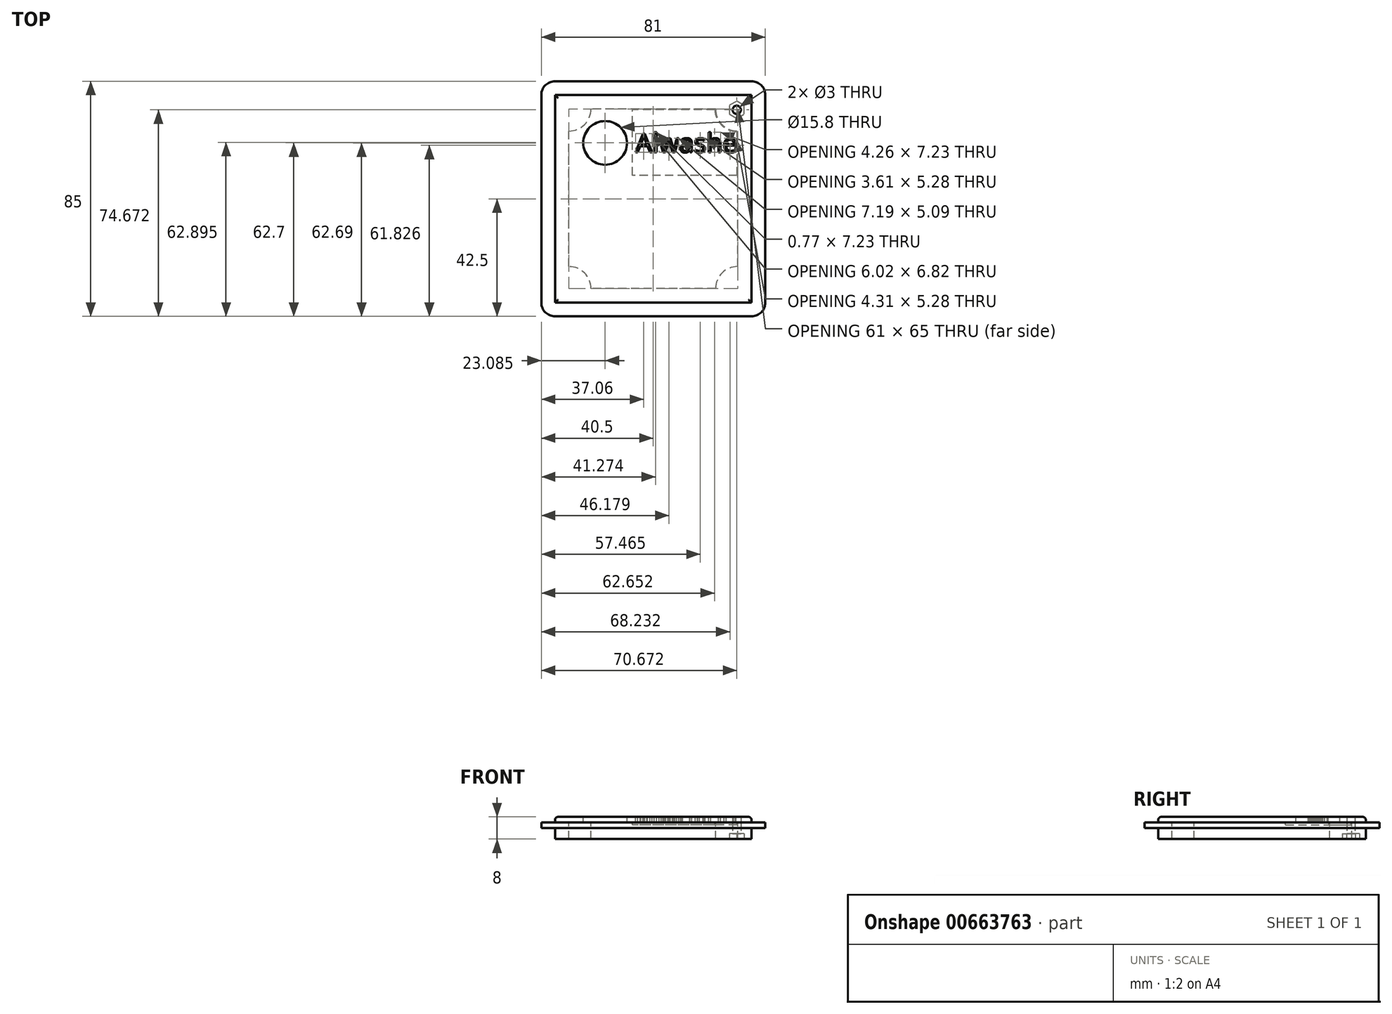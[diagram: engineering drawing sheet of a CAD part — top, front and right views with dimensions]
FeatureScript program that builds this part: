
annotation { "Feature Type Name" : "Feature", "Feature Type Description" : "" }
export const myFeature = defineFeature(function(context is Context, id is Id, definition is map)
    precondition{}
    {
        {
            var Q0;
            Q0=qCreatedBy(makeId("Top.planeOp"),FACE);
            var sketch = newSketch(context, id + "F0", { "sketchPlane" : qUnion([Q0])});
            skLineSegment(sketch, "E0.bottom", {"start": v(35.5, -37.5) * mm, "end": v(-35.5, -37.5) * mm});
            skLineSegment(sketch, "E0.top", {"start": v(35.5, 37.5) * mm, "end": v(-35.5, 37.5) * mm});
            skLineSegment(sketch, "E0.left", {"start": v(35.5, -37.5) * mm, "end": v(35.5, 37.5) * mm});
            skLineSegment(sketch, "E0.right", {"start": v(-35.5, -37.5) * mm, "end": v(-35.5, 37.5) * mm});
            skPoint(sketch, "E0.middle", {"position": v(0, 0) * mm});
            skSolve(sketch);
        }
        {
            var Q0;
            Q0 = qSketchRegion(id + "F0", true);
            extrude(context, id + "F1", {"entities" : qUnion([Q0]), "depth" : 4 * mm, "offsetDistance" : 25 * mm});
        }
        {
            var Q0;
            Q0=makeQuery(id+"F1.opExtrude","CAP_FACE",FACE,{"disambiguationData":[OSD([sQuery(id+"F0.wireOp",EDGE,"E0.bottom"),sQuery(id+"F0.wireOp",EDGE,"E0.top"),sQuery(id+"F0.wireOp",EDGE,"E0.left"),sQuery(id+"F0.wireOp",EDGE,"E0.right")])],"isStart":false});
            var sketch = newSketch(context, id + "F2", { "sketchPlane" : qUnion([Q0])});
            skLineSegment(sketch, "E1.bottom", {"start": v(30.5, -32.5) * mm, "end": v(22.5, -32.5) * mm, "construction": true});
            skLineSegment(sketch, "E1.top", {"start": v(30.5, 32.5) * mm, "end": v(22.5, 32.5) * mm, "construction": true});
            skLineSegment(sketch, "E1.left", {"start": v(30.5, -32.5) * mm, "end": v(30.5, -24.5) * mm, "construction": true});
            skLineSegment(sketch, "E1.right", {"start": v(-30.5, -32.5) * mm, "end": v(-30.5, -24.5) * mm, "construction": true});
            skPoint(sketch, "E1.middle", {"position": v(0, 0) * mm});
            skArc(sketch, "E2", {"start": v(-30.5, 24.5) * mm, "mid": v(-24.84, 26.84) * mm, "end": v(-22.5, 32.5) * mm});
            skLineSegment(sketch, "E3", {"start": v(-22.5, 32.5) * mm, "end": v(-30.5, 32.5) * mm, "construction": true});
            skLineSegment(sketch, "E4", {"start": v(-30.5, 24.5) * mm, "end": v(-30.5, 32.5) * mm, "construction": true});
            skArc(sketch, "E5.MirrorCS", {"start": v(30.5, 24.5) * mm, "mid": v(24.84, 26.84) * mm, "end": v(22.5, 32.5) * mm});
            skArc(sketch, "E6.MirrorCS", {"start": v(-30.5, -24.5) * mm, "mid": v(-24.84, -26.84) * mm, "end": v(-22.5, -32.5) * mm});
            skArc(sketch, "E7.MirrorCS", {"start": v(30.5, -24.5) * mm, "mid": v(24.84, -26.84) * mm, "end": v(22.5, -32.5) * mm});
            skLineSegment(sketch, "E8", {"start": v(-30.5, -24.5) * mm, "end": v(-30.5, 24.5) * mm});
            skLineSegment(sketch, "E9", {"start": v(-22.5, -32.5) * mm, "end": v(-30.5, -32.5) * mm, "construction": true});
            skLineSegment(sketch, "E10", {"start": v(22.5, -32.5) * mm, "end": v(-22.5, -32.5) * mm});
            skLineSegment(sketch, "E11", {"start": v(30.5, -24.5) * mm, "end": v(30.5, 24.5) * mm});
            skLineSegment(sketch, "E12", {"start": v(30.5, 24.5) * mm, "end": v(30.5, 32.5) * mm, "construction": true});
            skLineSegment(sketch, "E13", {"start": v(22.5, 32.5) * mm, "end": v(-22.5, 32.5) * mm});
            skSolve(sketch);
        }
        {
            var Q0;
            Q0=makeQuery(id+"F2.imprint","IMPRINT",FACE,{"disambiguationData":[TD([[makeQuery(id+"F2.imprint","IMPRINT",EDGE,{"derivedFrom":sQuery(id+"F2.wireOp",EDGE,"E2")}),-1.0]])]});
            extrude(context, id + "F3", {"entities" : qUnion([Q0]), "operationType" : NewBodyOperationType.REMOVE, "oppositeDirection" : true, "depth" : 25 * mm, "offsetDistance" : 25 * mm});
        }
        {
            var Q0;
            Q0=makeQuery(id+"F1.opExtrude","CAP_FACE",FACE,{"disambiguationData":[OSD([sQuery(id+"F0.wireOp",EDGE,"E0.bottom"),sQuery(id+"F0.wireOp",EDGE,"E0.top"),sQuery(id+"F0.wireOp",EDGE,"E0.left"),sQuery(id+"F0.wireOp",EDGE,"E0.right")])],"isStart":false});
            var sketch = newSketch(context, id + "F4", { "sketchPlane" : qUnion([Q0])});
            skLineSegment(sketch, "E14.bottom", {"start": v(35.5, -42.5) * mm, "end": v(-35.5, -42.5) * mm});
            skLineSegment(sketch, "E14.top", {"start": v(35.5, 42.5) * mm, "end": v(-35.5, 42.5) * mm});
            skLineSegment(sketch, "E14.left", {"start": v(40.5, -37.5) * mm, "end": v(40.5, 37.5) * mm});
            skLineSegment(sketch, "E14.right", {"start": v(-40.5, -37.5) * mm, "end": v(-40.5, 37.5) * mm});
            skPoint(sketch, "E14.middle", {"position": v(0, 0) * mm});
            skPoint(sketch, "E15.visualSharp", {"position": v(-40.5, 42.5) * mm});
            skArc(sketch, "E15.filletArc", {"start": v(-35.5, 42.5) * mm, "mid": v(-39.04, 41.04) * mm, "end": v(-40.5, 37.5) * mm});
            skPoint(sketch, "E16.visualSharp", {"position": v(40.5, 42.5) * mm});
            skArc(sketch, "E16.filletArc", {"start": v(40.5, 37.5) * mm, "mid": v(39.04, 41.04) * mm, "end": v(35.5, 42.5) * mm});
            skPoint(sketch, "E17.visualSharp", {"position": v(40.5, -42.5) * mm});
            skArc(sketch, "E17.filletArc", {"start": v(35.5, -42.5) * mm, "mid": v(39.04, -41.04) * mm, "end": v(40.5, -37.5) * mm});
            skPoint(sketch, "E18.visualSharp", {"position": v(-40.5, -42.5) * mm});
            skArc(sketch, "E18.filletArc", {"start": v(-40.5, -37.5) * mm, "mid": v(-39.04, -41.04) * mm, "end": v(-35.5, -42.5) * mm});
            skArc(sketch, "E19.0", {"start": v(-30.5, 24.5) * mm, "mid": v(-24.84, 26.84) * mm, "end": v(-22.5, 32.5) * mm});
            skLineSegment(sketch, "E19.1", {"start": v(22.5, 32.5) * mm, "end": v(-22.5, 32.5) * mm});
            skArc(sketch, "E19.2", {"start": v(30.5, 24.5) * mm, "mid": v(24.84, 26.84) * mm, "end": v(22.5, 32.5) * mm});
            skLineSegment(sketch, "E19.3", {"start": v(30.5, -24.5) * mm, "end": v(30.5, 24.5) * mm});
            skArc(sketch, "E19.4", {"start": v(30.5, -24.5) * mm, "mid": v(24.84, -26.84) * mm, "end": v(22.5, -32.5) * mm});
            skLineSegment(sketch, "E19.5", {"start": v(22.5, -32.5) * mm, "end": v(-22.5, -32.5) * mm});
            skArc(sketch, "E19.6", {"start": v(-30.5, -24.5) * mm, "mid": v(-24.84, -26.84) * mm, "end": v(-22.5, -32.5) * mm});
            skLineSegment(sketch, "E19.7", {"start": v(-30.5, -24.5) * mm, "end": v(-30.5, 24.5) * mm});
            skSolve(sketch);
        }
        {
            var Q0;
            Q0 = qSketchRegion(id + "F4", true);
            extrude(context, id + "F5", {"entities" : qUnion([Q0]), "operationType" : NewBodyOperationType.ADD, "depth" : 2 * mm, "offsetDistance" : 25 * mm});
        }
        {
            var Q0;
            Q0=makeQuery(id+"F1.opExtrude","CAP_FACE",FACE,{"disambiguationData":[OSD([sQuery(id+"F0.wireOp",EDGE,"E0.bottom"),sQuery(id+"F0.wireOp",EDGE,"E0.top"),sQuery(id+"F0.wireOp",EDGE,"E0.left"),sQuery(id+"F0.wireOp",EDGE,"E0.right")])],"isStart":true});
            var sketch = newSketch(context, id + "F6", { "sketchPlane" : qUnion([Q0])});
            skLineSegment(sketch, "E20", {"start": v(35.5, -37.5) * mm, "end": v(24.84, -26.84) * mm, "construction": true});
            skCircle(sketch, "E21.cCircle", {"center": v(30.17, -32.17) * mm, "radius": 2.7 * mm, "construction": true});
            skLineSegment(sketch, "E21.0", {"start": v(27.47, -33.73) * mm, "end": v(27.47, -30.61) * mm});
            skLineSegment(sketch, "E21.1", {"start": v(27.47, -30.61) * mm, "end": v(30.17, -29.05) * mm});
            skLineSegment(sketch, "E21.2", {"start": v(30.17, -29.05) * mm, "end": v(32.87, -30.61) * mm});
            skLineSegment(sketch, "E21.3", {"start": v(32.87, -30.61) * mm, "end": v(32.87, -33.73) * mm});
            skLineSegment(sketch, "E21.4", {"start": v(32.87, -33.73) * mm, "end": v(30.17, -35.29) * mm});
            skLineSegment(sketch, "E21.5", {"start": v(30.17, -35.29) * mm, "end": v(27.47, -33.73) * mm});
            skPoint(sketch, "E21.0.midPoint", {"position": v(27.47, -32.17) * mm});
            skSolve(sketch);
        }
        {
            var Q0;
            Q0 = qSketchRegion(id + "F6", true);
            extrude(context, id + "F7", {"entities" : qUnion([Q0]), "operationType" : NewBodyOperationType.REMOVE, "oppositeDirection" : true, "depth" : 2 * mm, "offsetDistance" : 25 * mm});
        }
        {
            var Q0;
            Q0=makeQuery(id+"F5.opExtrude","CAP_FACE",FACE,{"disambiguationData":[OSD([sQuery(id+"F4.wireOp",EDGE,"E14.bottom"),sQuery(id+"F4.wireOp",EDGE,"E14.top"),sQuery(id+"F4.wireOp",EDGE,"E14.left"),sQuery(id+"F4.wireOp",EDGE,"E14.right"),sQuery(id+"F4.wireOp",EDGE,"E15.filletArc"),sQuery(id+"F4.wireOp",EDGE,"E16.filletArc"),sQuery(id+"F4.wireOp",EDGE,"E17.filletArc"),sQuery(id+"F4.wireOp",EDGE,"E18.filletArc"),sQuery(id+"F4.wireOp",EDGE,"E19.0"),sQuery(id+"F4.wireOp",EDGE,"E19.1"),sQuery(id+"F4.wireOp",EDGE,"E19.2"),sQuery(id+"F4.wireOp",EDGE,"E19.3"),sQuery(id+"F4.wireOp",EDGE,"E19.4"),sQuery(id+"F4.wireOp",EDGE,"E19.5"),sQuery(id+"F4.wireOp",EDGE,"E19.6"),sQuery(id+"F4.wireOp",EDGE,"E19.7")])],"isStart":false});
            var sketch = newSketch(context, id + "F8", { "sketchPlane" : qUnion([Q0])});
            skLineSegment(sketch, "E22.bottom", {"start": v(-35.5, 37.5) * mm, "end": v(35.5, 37.5) * mm});
            skLineSegment(sketch, "E22.top", {"start": v(-35.5, -37.5) * mm, "end": v(35.5, -37.5) * mm});
            skLineSegment(sketch, "E22.left", {"start": v(-35.5, 37.5) * mm, "end": v(-35.5, -37.5) * mm});
            skLineSegment(sketch, "E22.right", {"start": v(35.5, 37.5) * mm, "end": v(35.5, -37.5) * mm});
            skPoint(sketch, "E22.middle", {"position": v(0, 0) * mm});
            skLineSegment(sketch, "E23", {"start": v(-30.5, 0) * mm, "end": v(-40.5, 0) * mm});
            skPoint(sketch, "E24", {"position": v(-35.5, 0) * mm});
            skLineSegment(sketch, "E25", {"start": v(0, -42.5) * mm, "end": v(0, -32.5) * mm, "construction": true});
            skPoint(sketch, "E26", {"position": v(0, -37.5) * mm});
            skSolve(sketch);
        }
        {
            var Q0;
            Q0 = qSketchRegion(id + "F8", true);
            extrude(context, id + "F9", {"entities" : qUnion([Q0]), "depth" : 2 * mm, "offsetDistance" : 25 * mm});
        }
        {
            var Q0;
            Q0=makeQuery(id+"F1.opExtrude","CAP_FACE",FACE,{"disambiguationData":[OSD([sQuery(id+"F0.wireOp",EDGE,"E0.bottom"),sQuery(id+"F0.wireOp",EDGE,"E0.top"),sQuery(id+"F0.wireOp",EDGE,"E0.left"),sQuery(id+"F0.wireOp",EDGE,"E0.right")])],"isStart":true});
            var sketch = newSketch(context, id + "F10", { "sketchPlane" : qUnion([Q0])});
            skPoint(sketch, "E27.0", {"position": v(30.17, -32.17) * mm});
            skCircle(sketch, "E28", {"center": v(30.17, -32.17) * mm, "radius": 1.5 * mm});
            skSolve(sketch);
        }
        {
            var Q0;
            Q0 = qSketchRegion(id + "F10", true);
            extrude(context, id + "F11", {"entities" : qUnion([Q0]), "operationType" : NewBodyOperationType.REMOVE, "oppositeDirection" : true, "depth" : 25 * mm, "offsetDistance" : 25 * mm});
        }
        {
            var Q0;
            Q0=makeQuery(id+"F9.opExtrude","CAP_FACE",FACE,{"disambiguationData":[OSD([sQuery(id+"F8.wireOp",EDGE,"E22.bottom"),sQuery(id+"F8.wireOp",EDGE,"E22.top"),sQuery(id+"F8.wireOp",EDGE,"E22.left"),sQuery(id+"F8.wireOp",EDGE,"E22.right")])],"isStart":false});
            var sketch = newSketch(context, id + "F12", { "sketchPlane" : qUnion([Q0])});
            skCircle(sketch, "E29", {"center": v(-17.41, 20.2) * mm, "radius": 7.9 * mm});
            skCircle(sketch, "E30", {"center": v(-17.41, 0) * mm, "radius": 7.9 * mm, "construction": true});
            skCircle(sketch, "E31", {"center": v(-17.41, -20.2) * mm, "radius": 7.9 * mm, "construction": true});
            skLineSegment(sketch, "E32.0", {"start": v(22.5, 32.5) * mm, "end": v(-22.5, 32.5) * mm, "construction": true});
            skLineSegment(sketch, "E32.1", {"start": v(22.5, -32.5) * mm, "end": v(-22.5, -32.5) * mm, "construction": true});
            skLineSegment(sketch, "E32.2", {"start": v(-30.5, -24.5) * mm, "end": v(-30.5, 24.5) * mm, "construction": true});
            skArc(sketch, "E32.3", {"start": v(-30.5, -24.5) * mm, "mid": v(-24.84, -26.84) * mm, "end": v(-22.5, -32.5) * mm, "construction": true});
            skArc(sketch, "E32.4", {"start": v(-30.5, 24.5) * mm, "mid": v(-24.84, 26.84) * mm, "end": v(-22.5, 32.5) * mm, "construction": true});
            skArc(sketch, "E32.5", {"start": v(30.5, 24.5) * mm, "mid": v(24.84, 26.84) * mm, "end": v(22.5, 32.5) * mm, "construction": true});
            skLineSegment(sketch, "E32.6", {"start": v(30.5, -24.5) * mm, "end": v(30.5, 24.5) * mm, "construction": true});
            skArc(sketch, "E32.7", {"start": v(30.5, -24.5) * mm, "mid": v(24.84, -26.84) * mm, "end": v(22.5, -32.5) * mm, "construction": true});
            skLineSegment(sketch, "E33", {"start": v(-17.41, 32.5) * mm, "end": v(-17.41, 7.9) * mm, "construction": true});
            skText(sketch, "E34", { "text": "Alwashe", "fontName": "OpenSans-Regular.ttf"});
            skPoint(sketch, "E35", {"position": v(-6.45, 20.2) * mm});
            const initialGuessF12  = {"E34": [-0.00645, 0.01678, 1, 0, 0.00685]};
            skSetInitialGuess(sketch, initialGuessF12);
            skSolve(sketch);
        }
        {
            var Q0;
            Q0 = qSketchRegion(id + "F12", true);
            extrude(context, id + "F13", {"entities" : qUnion([Q0]), "operationType" : NewBodyOperationType.REMOVE, "oppositeDirection" : true, "depth" : 25 * mm, "offsetDistance" : 25 * mm});
        }
        {
            var Q0;
            {var subQ0=sQuery(id+"F8.wireOp",EDGE,"E22.right");var subQ1=sQuery(id+"F8.wireOp",EDGE,"E22.left");var subQ2=sQuery(id+"F8.wireOp",EDGE,"E22.top");var subQ3=sQuery(id+"F8.wireOp",EDGE,"E22.bottom");var subQ4=makeQuery(id+"F9.opExtrude","CAP_FACE",FACE,{"disambiguationData":[OSD([subQ3,subQ2,subQ1,subQ0])],"isStart":true});Q0=makeQuery(id+"F13.boolean.opBoolean","SPLIT",FACE,{"disambiguationData":[TD([makeQuery(id+"F9.opExtrude","SWEPT_FACE",FACE,{"disambiguationData":[OSD([subQ3])]})])],"derivedFrom":subQ4});}
            var sketch = newSketch(context, id + "F14", { "sketchPlane" : qUnion([Q0])});
            skArc(sketch, "E36.0", {"start": v(30.5, -24.5) * mm, "mid": v(24.84, -26.84) * mm, "end": v(22.5, -32.5) * mm, "construction": true});
            skLineSegment(sketch, "E36.1", {"start": v(22.5, -32.5) * mm, "end": v(-22.5, -32.5) * mm, "construction": true});
            skLineSegment(sketch, "E36.2", {"start": v(30.5, 24.5) * mm, "end": v(30.5, -24.5) * mm, "construction": true});
            skLineSegment(sketch, "E37.0", {"start": v(22.25, -32.25) * mm, "end": v(-7.52, -32.25) * mm});
            skArc(sketch, "E37.1", {"start": v(30.25, -24.25) * mm, "mid": v(24.67, -26.67) * mm, "end": v(22.25, -32.25) * mm});
            skLineSegment(sketch, "E38", {"start": v(30.25, -8.5) * mm, "end": v(30.25, -24.25) * mm});
            skLineSegment(sketch, "E39", {"start": v(30.25, -8.5) * mm, "end": v(-7.52, -8.5) * mm});
            skLineSegment(sketch, "E40", {"start": v(-7.52, -8.5) * mm, "end": v(-7.52, -32.25) * mm});
            skSolve(sketch);
        }
        {
            var Q0;
            Q0 = qSketchRegion(id + "F14", true);
            var Q1;
            Q1 = qConstructionFilter(qBodyType(qCreatedBy(id + "F14" ,EDGE), BodyType.WIRE), ConstructionObject.NO);
            extrude(context, id + "F15", {"entities" : qUnion([Q0]), "surfaceEntities" : qUnion([Q1]), "depth" : 0.9 * mm, "offsetDistance" : 25 * mm});
        }
        {
            var Q0;
            Q0=makeQuery(id+"F9.opExtrude","CAP_EDGE",EDGE,{"disambiguationData":[OSD([sQuery(id+"F8.wireOp",EDGE,"E22.top")])],"isStart":false});
            var Q1;
            Q1=makeQuery(id+"F9.opExtrude","CAP_EDGE",EDGE,{"disambiguationData":[OSD([sQuery(id+"F8.wireOp",EDGE,"E22.left")])],"isStart":false});
            var Q2;
            Q2=makeQuery(id+"F9.opExtrude","CAP_EDGE",EDGE,{"disambiguationData":[OSD([sQuery(id+"F8.wireOp",EDGE,"E22.right")])],"isStart":false});
            var Q3;
            Q3=makeQuery(id+"F9.opExtrude","CAP_EDGE",EDGE,{"disambiguationData":[OSD([sQuery(id+"F8.wireOp",EDGE,"E22.bottom")])],"isStart":false});
            fillet(context, id + "F16", {"entities" : qUnion([Q0, Q1, Q2, Q3]), "radius" : 1 * mm, "tangentPropagation" : true, "allowEdgeOverflow" : false});
        }
    });
